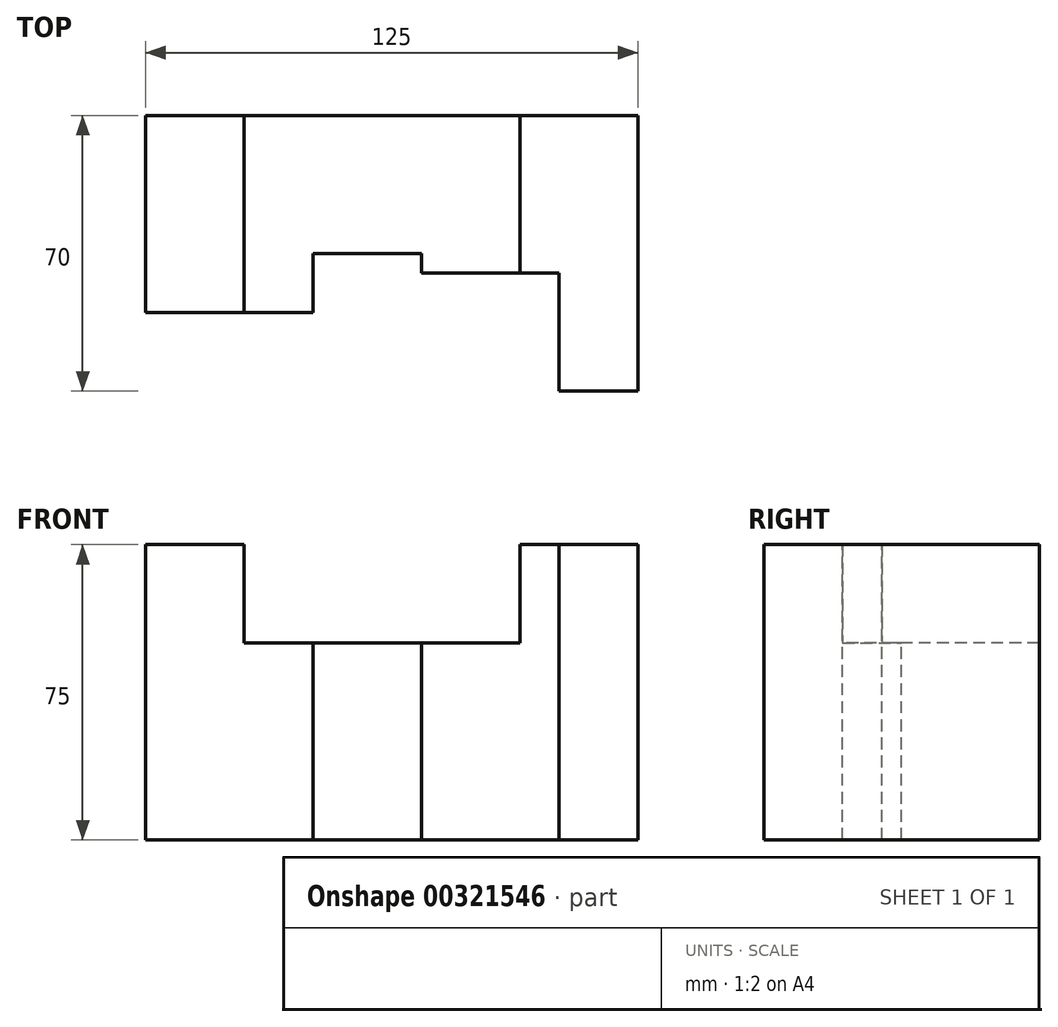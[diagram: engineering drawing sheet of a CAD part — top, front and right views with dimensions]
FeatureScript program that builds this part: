
annotation { "Feature Type Name" : "Feature", "Feature Type Description" : "" }
export const myFeature = defineFeature(function(context is Context, id is Id, definition is map)
    precondition{}
    {
        {
            var Q0;
            Q0=qCreatedBy(makeId("Front.planeOp"),FACE);
            var sketch = newSketch(context, id + "F0", { "sketchPlane" : qUnion([Q0])});
            skLineSegment(sketch, "E0.bottom", {"start": v(0, 0) * mm, "end": v(125, 0) * mm});
            skLineSegment(sketch, "E0.top", {"start": v(0, 75) * mm, "end": v(125, 75) * mm});
            skLineSegment(sketch, "E0.left", {"start": v(0, 0) * mm, "end": v(0, 75) * mm});
            skLineSegment(sketch, "E0.right", {"start": v(125, 0) * mm, "end": v(125, 75) * mm});
            skSolve(sketch);
        }
        {
            var Q0;
            Q0 = qSketchRegion(id + "F0", true);
            extrude(context, id + "F1", {"entities" : qUnion([Q0]), "depth" : 70 * mm});
        }
        {
            var Q0;
            Q0=makeQuery(id+"F1.opExtrude","CAP_FACE",FACE,{"disambiguationData":[OSD([sQuery(id+"F0.wireOp",EDGE,"E0.bottom"),sQuery(id+"F0.wireOp",EDGE,"E0.top"),sQuery(id+"F0.wireOp",EDGE,"E0.left"),sQuery(id+"F0.wireOp",EDGE,"E0.right")])],"isStart":false});
            var sketch = newSketch(context, id + "F2", { "sketchPlane" : qUnion([Q0])});
            skLineSegment(sketch, "E1.bottom", {"start": v(25, 75) * mm, "end": v(95, 75) * mm});
            skLineSegment(sketch, "E1.top", {"start": v(25, 50) * mm, "end": v(95, 50) * mm});
            skLineSegment(sketch, "E1.left", {"start": v(25, 75) * mm, "end": v(25, 50) * mm});
            skLineSegment(sketch, "E1.right", {"start": v(95, 75) * mm, "end": v(95, 50) * mm});
            skSolve(sketch);
        }
        {
            var Q0;
            Q0 = qSketchRegion(id + "F2", true);
            extrude(context, id + "F3", {"entities" : qUnion([Q0]), "operationType" : NewBodyOperationType.REMOVE, "endBound" : BoundingType.THROUGH_ALL, "oppositeDirection" : true, "depth" : 25 * mm});
        }
        {
            var Q0;
            {var subQ1=sQuery(id+"F0.wireOp",EDGE,"E0.left");var subQ2=sQuery(id+"F0.wireOp",EDGE,"E0.top");Q0=makeQuery(id+"F3.boolean.opBoolean","SPLIT",FACE,{"disambiguationData":[TD([makeQuery(id+"F1.opExtrude","SWEPT_FACE",FACE,{"disambiguationData":[OSD([subQ1])]})])],"derivedFrom":makeQuery(id+"F1.opExtrude","SWEPT_FACE",FACE,{"disambiguationData":[OSD([subQ2])]})});}
            var sketch = newSketch(context, id + "F4", { "sketchPlane" : qUnion([Q0])});
            skLineSegment(sketch, "E2", {"start": v(0, -70) * mm, "end": v(105, -70) * mm});
            skLineSegment(sketch, "E3", {"start": v(105, -70) * mm, "end": v(105, -40) * mm});
            skLineSegment(sketch, "E4", {"start": v(105, -40) * mm, "end": v(70, -40) * mm});
            skLineSegment(sketch, "E5", {"start": v(70, -40) * mm, "end": v(70, -35) * mm});
            skLineSegment(sketch, "E6", {"start": v(70, -35) * mm, "end": v(42.5, -35) * mm});
            skLineSegment(sketch, "E7", {"start": v(42.5, -35) * mm, "end": v(42.5, -50) * mm});
            skLineSegment(sketch, "E8", {"start": v(0, -50) * mm, "end": v(0, -70) * mm});
            skLineSegment(sketch, "E9", {"start": v(42.5, -50) * mm, "end": v(0, -50) * mm});
            skSolve(sketch);
        }
        {
            var Q0;
            Q0 = qSketchRegion(id + "F4", true);
            extrude(context, id + "F5", {"entities" : qUnion([Q0]), "operationType" : NewBodyOperationType.REMOVE, "endBound" : BoundingType.THROUGH_ALL, "oppositeDirection" : true, "depth" : 25 * mm});
        }
    });
